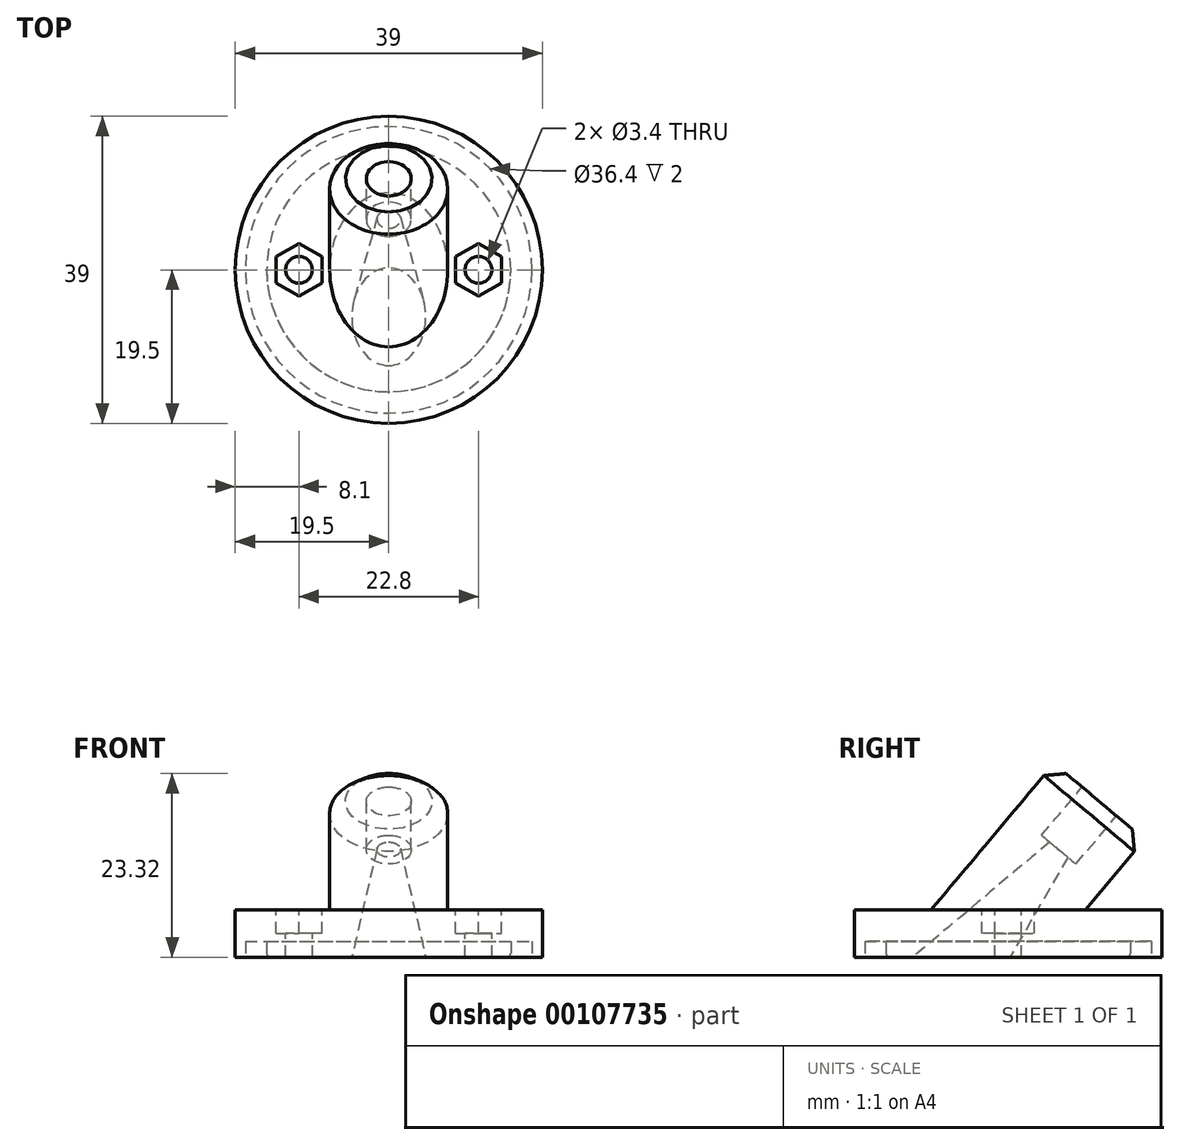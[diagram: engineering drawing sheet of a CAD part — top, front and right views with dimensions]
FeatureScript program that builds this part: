
annotation { "Feature Type Name" : "Feature", "Feature Type Description" : "" }
export const myFeature = defineFeature(function(context is Context, id is Id, definition is map)
    precondition{}
    {
        {
            var Q0;
            Q0=qCreatedBy(makeId("Top.planeOp"),FACE);
            var sketch = newSketch(context, id + "F0", { "sketchPlane" : qUnion([Q0])});
            skPoint(sketch, "E0.middle", {"position": v(0, 0) * mm});
            skLineSegment(sketch, "E1", {"start": v(-19.5, 0) * mm, "end": v(19.5, 0) * mm, "construction": true});
            skCircle(sketch, "E2", {"center": v(0, 0) * mm, "radius": 7.5 * mm, "construction": true});
            skCircle(sketch, "E3.cCircle", {"center": v(-11.4, 0) * mm, "radius": 2.9 * mm, "construction": true});
            skLineSegment(sketch, "E3.0", {"start": v(-8.5, -1.67) * mm, "end": v(-11.4, -3.35) * mm});
            skLineSegment(sketch, "E3.1", {"start": v(-11.4, -3.35) * mm, "end": v(-14.3, -1.67) * mm});
            skLineSegment(sketch, "E3.2", {"start": v(-14.3, -1.67) * mm, "end": v(-14.3, 1.67) * mm});
            skLineSegment(sketch, "E3.3", {"start": v(-14.3, 1.67) * mm, "end": v(-11.4, 3.35) * mm});
            skLineSegment(sketch, "E3.4", {"start": v(-11.4, 3.35) * mm, "end": v(-8.5, 1.67) * mm});
            skLineSegment(sketch, "E3.5", {"start": v(-8.5, 1.67) * mm, "end": v(-8.5, -1.67) * mm});
            skPoint(sketch, "E3.0.midPoint", {"position": v(-9.95, -2.51) * mm});
            skCircle(sketch, "E4", {"center": v(-11.4, 0) * mm, "radius": 1.7 * mm});
            skLineSegment(sketch, "E5", {"start": v(0, 7.5) * mm, "end": v(0, -7.5) * mm, "construction": true});
            skLineSegment(sketch, "E6.MirrorCS", {"start": v(8.5, -1.67) * mm, "end": v(11.4, -3.35) * mm});
            skLineSegment(sketch, "E7.MirrorCS", {"start": v(8.5, 1.67) * mm, "end": v(8.5, -1.67) * mm});
            skPoint(sketch, "E8.MirrorP", {"position": v(9.95, -2.51) * mm});
            skLineSegment(sketch, "E9.MirrorCS", {"start": v(11.4, -3.35) * mm, "end": v(14.3, -1.67) * mm});
            skLineSegment(sketch, "E10.MirrorCS", {"start": v(11.4, 3.35) * mm, "end": v(8.5, 1.67) * mm});
            skCircle(sketch, "E11.MirrorC", {"center": v(11.4, 0) * mm, "radius": 2.9 * mm, "construction": true});
            skLineSegment(sketch, "E12.MirrorCS", {"start": v(14.3, -1.67) * mm, "end": v(14.3, 1.67) * mm});
            skLineSegment(sketch, "E13.MirrorCS", {"start": v(14.3, 1.67) * mm, "end": v(11.4, 3.35) * mm});
            skCircle(sketch, "E14.MirrorC", {"center": v(11.4, 0) * mm, "radius": 1.7 * mm});
            skCircle(sketch, "E15", {"center": v(0, 0) * mm, "radius": 19.5 * mm});
            skSolve(sketch);
        }
        {
            var Q0;
            Q0=makeQuery(id+"F0.imprint","IMPRINT",FACE,{"disambiguationData":[TD([[makeQuery(id+"F0.imprint","IMPRINT",EDGE,{"derivedFrom":sQuery(id+"F0.wireOp",EDGE,"E0.bottom")}),-1.0]])]});
            var Q1;
            Q1=makeQuery(id+"F0.imprint","IMPRINT",FACE,{"disambiguationData":[TD([[makeQuery(id+"F0.imprint","IMPRINT",EDGE,{"derivedFrom":sQuery(id+"F0.wireOp",EDGE,"E3.0")}),-1.0]])]});
            var Q2;
            Q2=makeQuery(id+"F0.imprint","IMPRINT",FACE,{"disambiguationData":[TD([[makeQuery(id+"F0.imprint","IMPRINT",EDGE,{"derivedFrom":sQuery(id+"F0.wireOp",EDGE,"E6.MirrorCS")}),1.0]])]});
            var Q3;
            Q3=makeQuery(id+"F0.imprint","IMPRINT",FACE,{"disambiguationData":[TD([[makeQuery(id+"F0.imprint","IMPRINT",EDGE,{"derivedFrom":sQuery(id+"F0.wireOp",EDGE,"E3.0")}),1.0]])]});
            extrude(context, id + "F1", {"entities" : qUnion([Q0, Q1, Q2, Q3]), "oppositeDirection" : true, "depth" : 6 * mm});
        }
        {
            var Q0;
            Q0=makeQuery(id+"F0.imprint","IMPRINT",FACE,{"disambiguationData":[TD([[makeQuery(id+"F0.imprint","IMPRINT",EDGE,{"derivedFrom":sQuery(id+"F0.wireOp",EDGE,"E3.0")}),-1.0]])]});
            var Q1;
            Q1=makeQuery(id+"F0.imprint","IMPRINT",FACE,{"disambiguationData":[TD([[makeQuery(id+"F0.imprint","IMPRINT",EDGE,{"derivedFrom":sQuery(id+"F0.wireOp",EDGE,"E6.MirrorCS")}),1.0]])]});
            extrude(context, id + "F2", {"entities" : qUnion([Q0, Q1]), "operationType" : NewBodyOperationType.REMOVE, "oppositeDirection" : true, "depth" : 3 * mm});
        }
        {
            var Q0;
            Q0=sQuery(id+"F0.wireOp",EDGE,"E1");
            cPlane(context, id + "F3", {"entities" : qUnion([Q0]), "cplaneType" : CPlaneType.LINE_ANGLE, "offset" : 150 * mm, "angle" : 50 * degree, "width" : 150 * mm, "height" : 150 * mm});
        }
        {
            var Q0;
            Q0=qCreatedBy(id+"F3.planeOp",FACE);
            var sketch = newSketch(context, id + "F4", { "sketchPlane" : qUnion([Q0])});
            skCircle(sketch, "E16", {"center": v(0, 0) * mm, "radius": 7.5 * mm});
            skSolve(sketch);
        }
        {
            var Q0;
            Q0=qSketchRegion(id+"F4",true);
            var Q1;
            Q1=makeQuery(id+"F1.opExtrude","CAP_FACE",FACE,{"disambiguationData":[OSD([sQuery(id+"F0.wireOp",EDGE,"E0.bottom"),sQuery(id+"F0.wireOp",EDGE,"E0.top"),sQuery(id+"F0.wireOp",EDGE,"E0.left"),sQuery(id+"F0.wireOp",EDGE,"E0.right"),sQuery(id+"F0.wireOp",EDGE,"E4"),sQuery(id+"F0.wireOp",EDGE,"E14.MirrorC")])],"isStart":true});
            extrude(context, id + "F5", {"entities" : qUnion([Q0]), "operationType" : NewBodyOperationType.ADD, "endBound" : BoundingType.UP_TO_SURFACE, "oppositeDirection" : true, "endBoundEntityFace" : qUnion([Q1]), "depth" : 25 * mm, "hasSecondDirection" : true, "secondDirectionOppositeDirection" : false, "secondDirectionDepth" : 18 * mm});
        }
        {
            var Q0;
            Q0=makeQuery(id+"F5.opExtrude","CAP_FACE",FACE,{"disambiguationData":[OSD([sQuery(id+"F4.wireOp",EDGE,"E16")])],"isStart":true});
            var sketch = newSketch(context, id + "F6", { "sketchPlane" : qUnion([Q0])});
            skCircle(sketch, "E17", {"center": v(0, 0) * mm, "radius": 2.85 * mm});
            skSolve(sketch);
        }
        {
            var Q0;
            Q0=qSketchRegion(id+"F6",true);
            extrude(context, id + "F7", {"entities" : qUnion([Q0]), "operationType" : NewBodyOperationType.REMOVE, "oppositeDirection" : true, "depth" : 8 * mm});
        }
        {
            var Q0;
            Q0=makeQuery(id+"F7.boolean.opBoolean","COPY",FACE,{"derivedFrom":makeQuery(id+"F7.opExtrude","CAP_FACE",FACE,{"disambiguationData":[OSD([sQuery(id+"F6.wireOp",EDGE,"E17")])],"isStart":false})});
            var sketch = newSketch(context, id + "F8", { "sketchPlane" : qUnion([Q0])});
            skCircle(sketch, "E18", {"center": v(0, 0) * mm, "radius": 1.5 * mm});
            skSolve(sketch);
        }
        {
            var Q0;
            Q0=qSketchRegion(id+"F8",true);
            var Q1;
            Q1=makeQuery(id+"F1.opExtrude","CAP_FACE",FACE,{"disambiguationData":[OSD([sQuery(id+"F0.wireOp",EDGE,"E0.bottom"),sQuery(id+"F0.wireOp",EDGE,"E0.top"),sQuery(id+"F0.wireOp",EDGE,"E0.left"),sQuery(id+"F0.wireOp",EDGE,"E0.right"),sQuery(id+"F0.wireOp",EDGE,"E4"),sQuery(id+"F0.wireOp",EDGE,"E14.MirrorC")])],"isStart":false});
            extrude(context, id + "F9", {"entities" : qUnion([Q0]), "operationType" : NewBodyOperationType.REMOVE, "endBound" : BoundingType.UP_TO_SURFACE, "oppositeDirection" : true, "endBoundEntityFace" : qUnion([Q1]), "depth" : 25 * mm, "hasDraft" : true, "draftAngle" : 10 * degree});
        }
        {
            var Q0;
            Q0=makeQuery(id+"F5.opExtrude","CAP_EDGE",EDGE,{"disambiguationData":[OSD([sQuery(id+"F4.wireOp",EDGE,"E16")])],"isStart":true});
            chamfer(context, id + "F10", {"entities" : qUnion([Q0]), "width" : 2 * mm, "tangentPropagation" : true});
        }
        {
            var Q0;
            Q0=makeQuery(id+"F1.opExtrude","CAP_FACE",FACE,{"disambiguationData":[OSD([sQuery(id+"F0.wireOp",EDGE,"E4"),sQuery(id+"F0.wireOp",EDGE,"E14.MirrorC"),sQuery(id+"F0.wireOp",EDGE,"E15")])],"isStart":false});
            var sketch = newSketch(context, id + "F11", { "sketchPlane" : qUnion([Q0])});
            skCircle(sketch, "E19", {"center": v(0, 0) * mm, "radius": 15.5 * mm});
            skCircle(sketch, "E20.0", {"center": v(0, 0) * mm, "radius": 18.2 * mm});
            skCircle(sketch, "E21", {"center": v(0, 5.95) * mm, "radius": 7 * mm});
            skCircle(sketch, "E22.0", {"center": v(0, 5.95) * mm, "radius": 9.5 * mm});
            skSolve(sketch);
        }
        {
            var Q0;
            Q0=makeQuery(id+"F11.imprint","IMPRINT",FACE,{"disambiguationData":[TD([[makeQuery(id+"F11.imprint","IMPRINT",EDGE,{"derivedFrom":sQuery(id+"F11.wireOp",EDGE,"E19")}),-1.0]])]});
            extrude(context, id + "F12", {"entities" : qUnion([Q0]), "operationType" : NewBodyOperationType.REMOVE, "oppositeDirection" : true, "depth" : 2 * mm});
        }
        {
            var Q0;
            Q0=makeQuery(id+"F12.boolean.opBoolean","COPY",EDGE,{"derivedFrom":makeQuery(id+"F12.opExtrude","CAP_EDGE",EDGE,{"disambiguationData":[OSD([sQuery(id+"F11.wireOp",EDGE,"E20.0")])],"isStart":true})});
            var Q1;
            Q1=makeQuery(id+"F12.boolean.opBoolean","COPY",EDGE,{"derivedFrom":makeQuery(id+"F12.opExtrude","CAP_EDGE",EDGE,{"disambiguationData":[OSD([sQuery(id+"F11.wireOp",EDGE,"E19")])],"isStart":true})});
            fillet(context, id + "F13", {"entities" : qUnion([Q0, Q1]), "radius" : 0.5 * mm, "tangentPropagation" : true, "allowEdgeOverflow" : false});
        }
    });
